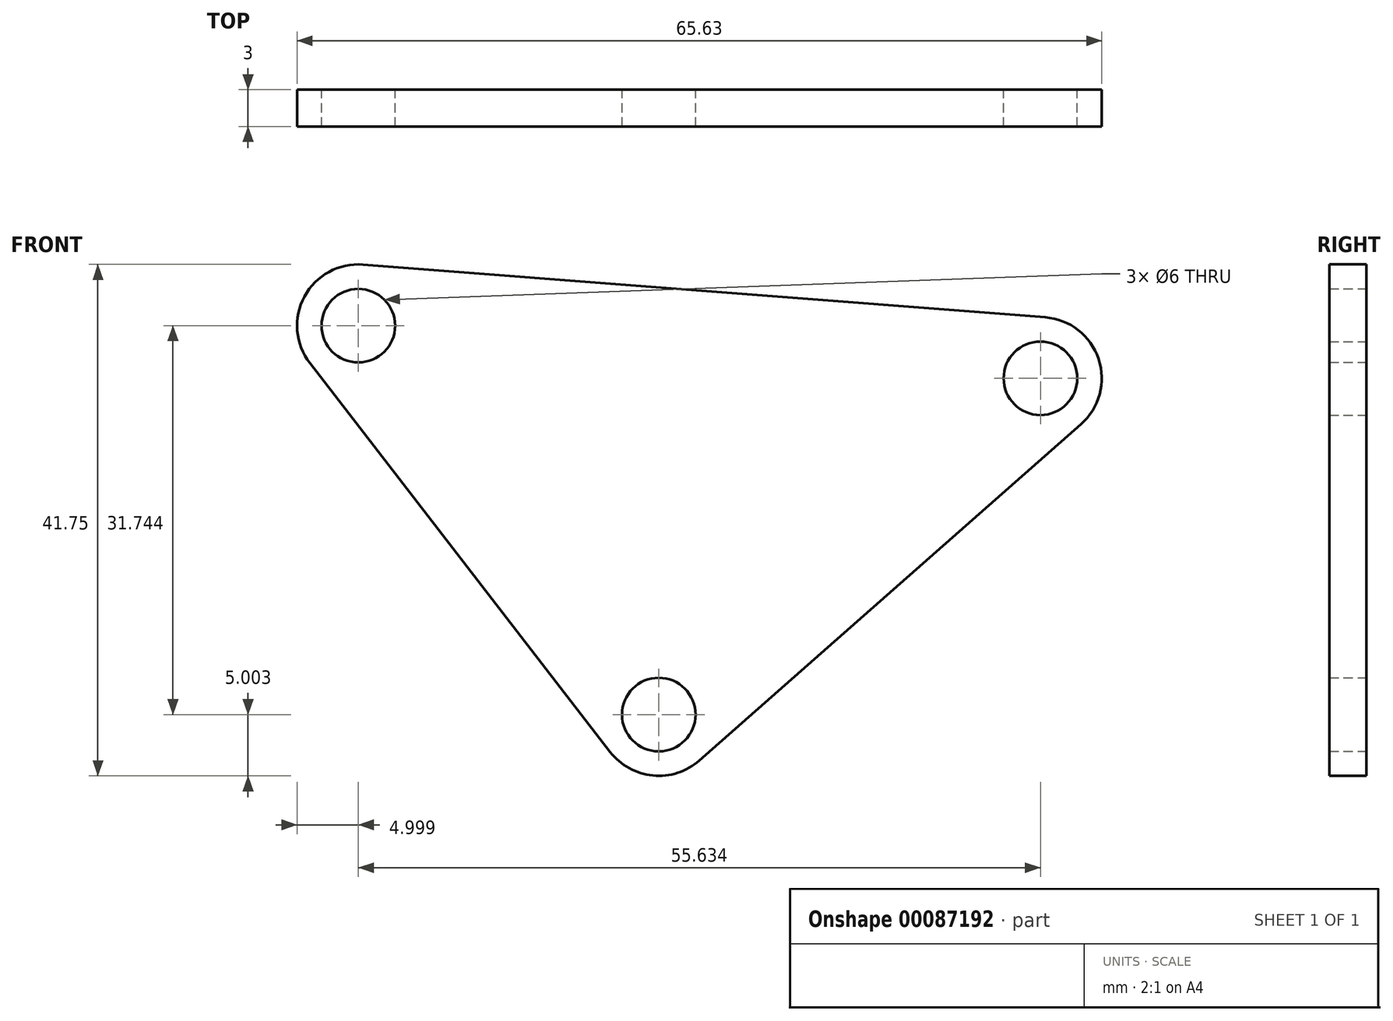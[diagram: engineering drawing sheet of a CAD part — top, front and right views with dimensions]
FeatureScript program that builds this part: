
annotation { "Feature Type Name" : "Feature", "Feature Type Description" : "" }
export const myFeature = defineFeature(function(context is Context, id is Id, definition is map)
    precondition{}
    {
        {
            var Q0;
            Q0=qCreatedBy(makeId("Front.planeOp"),FACE);
            var sketch = newSketch(context, id + "F0", { "sketchPlane" : qUnion([Q0])});
            skLineSegment(sketch, "E0", {"start": v(-37.76, 5.26) * mm, "end": v(-6.63, 32.7) * mm, "construction": true});
            skLineSegment(sketch, "E1", {"start": v(-6.63, 32.7) * mm, "end": v(-62.26, 37) * mm, "construction": true});
            skLineSegment(sketch, "E2", {"start": v(-62.26, 37) * mm, "end": v(-37.76, 5.26) * mm, "construction": true});
            skCircle(sketch, "E3", {"center": v(-62.26, 37) * mm, "radius": 3 * mm});
            skCircle(sketch, "E4", {"center": v(-6.63, 32.7) * mm, "radius": 3 * mm});
            skCircle(sketch, "E5", {"center": v(-37.76, 5.26) * mm, "radius": 3 * mm});
            skLineSegment(sketch, "E6", {"start": v(-6.24, 37.69) * mm, "end": v(-61.88, 42) * mm});
            skLineSegment(sketch, "E7", {"start": v(-66.22, 33.95) * mm, "end": v(-41.72, 2.2) * mm});
            skLineSegment(sketch, "E8", {"start": v(-34.45, 1.51) * mm, "end": v(-3.32, 28.95) * mm});
            skPoint(sketch, "E9.visualSharp", {"position": v(5.55, 36.78) * mm});
            skArc(sketch, "E9.filletArc", {"start": v(-3.32, 28.95) * mm, "mid": v(-1.89, 34.29) * mm, "end": v(-6.24, 37.69) * mm});
            skPoint(sketch, "E10.visualSharp", {"position": v(-73.1, 42.86) * mm});
            skArc(sketch, "E10.filletArc", {"start": v(-61.88, 42) * mm, "mid": v(-66.66, 39.38) * mm, "end": v(-66.22, 33.95) * mm});
            skPoint(sketch, "E11.visualSharp", {"position": v(-38.46, -2.02) * mm});
            skArc(sketch, "E11.filletArc", {"start": v(-41.72, 2.2) * mm, "mid": v(-38.24, 0.29) * mm, "end": v(-34.45, 1.51) * mm});
            skSolve(sketch);
        }
        {
            var Q0;
            Q0 = qSketchRegion(id + "F0", true);
            extrude(context, id + "F1", {"entities" : qUnion([Q0]), "depth" : 3 * mm});
        }
    });
